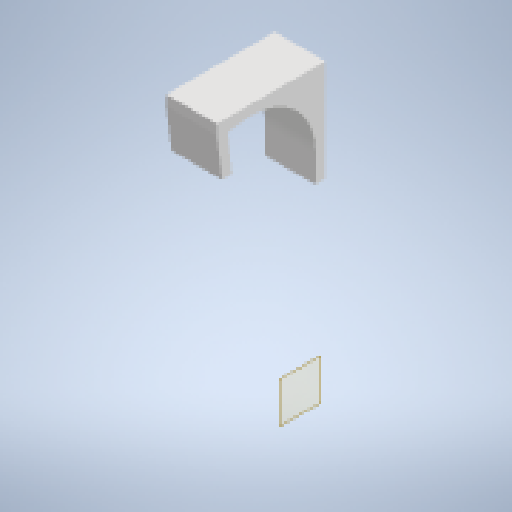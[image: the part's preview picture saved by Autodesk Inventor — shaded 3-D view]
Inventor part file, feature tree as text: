
AUTODESK INVENTOR PART (.ipt)
format: ipt  version: 2023 (Build 270158000, 158)  size: 165,376 bytes
history: native  units: mm
features: other x4, extrude x2, reference x2, plane x1, sketch x1, fillet x1
ambient origin geometry x8: Origin, YZ Plane, XZ Plane, XY Plane, X Axis, Y Axis, Z Axis, Center Point
bodies: Solid1 (feature_tree)
feature tree (11):
  plane  "Work Plane1"
  sketch  "Sketch2"  dims[d0=78.575mm d2=5.0mm d3=20.0mm d4=50.0mm d5=5.0mm d6=5.0mm d7=40.0mm d8=5.0mm d9=0.95mm d10=25.0mm d11=0.0mm d12=13.2mm d13=0.0mm d14=31.25mm]
  extrude  "Extrusion1"  Depth=5.0mm
  extrude  "Extrusion2"  Depth=20.0mm
  fillet  "Fillet1"  Radius=50.0mm
  reference  "Reference1"
  reference  "Reference2"
  parser-record x1  (decoder bookkeeping rows leaked as tree rows — omitted from the tree; the rows remain in map.json)
  other  "Assembly.iam"
  other  "Album:1"
  other  "wall:1"
note: 1 file-system path scrubbed to <path> (originals preserved in map.json)
